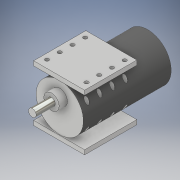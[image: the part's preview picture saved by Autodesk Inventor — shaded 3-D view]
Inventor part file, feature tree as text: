
AUTODESK INVENTOR PART (.ipt)
format: ipt  version: 2019 (Build 230136000, 136)  size: 185,856 bytes
history: native  units: in
note: dims shown in document units (in); Inventor stores cm internally (conversion verified against a paired STEP export)
features: sketch x5, extrude x4, plane x1, hole x1, pattern_linear x1, mirror x1
ambient origin geometry x8: Origin, YZ Plane, XZ Plane, XY Plane, X Axis, Y Axis, Z Axis, Center Point
bodies: Solid1 (feature_tree)
feature tree (13):
  extrude  "Extrusion1"  Depth=2.7165in TaperAngle=0.0deg
  extrude  "Extrusion2"  Depth=0.685in
  extrude  "Extrusion3"  Depth=0.2559in TaperAngle=0.0deg
  plane  "Work Plane1"
  extrude  "Extrusion4"  Depth=0.5906in TaperAngle=0.0deg
  hole  "Hole1"  [1 undecoded]
  pattern_linear  "Rectangular Pattern1"  Spacing1=1.6142in  [1 undecoded]
  mirror  "Mirror1"
  sketch  "Sketch1"  dims[d0=1.4567in d1=2.7165in d2=0.0in]
  sketch  "Sketch2"  dims[d5=0.7283in d6=0.685in]
  sketch  "Sketch3"  dims[d7=0.2362in d8=0.2559in d9=0.0in]
  sketch  "Sketch4"  dims[d10=0.2362in d11=0.5906in d12=0.0in]
  sketch  "Sketch5"  dims[d13=2.7362in d14=0.7874in d15=1.6142in d16=1.5748in d17=1.6142in d18=0.1378in d19=0.0in d20=0.1772in d21=0.2362in d22=0.3937in d23=90.0deg d24=0.1772in d25=0.2362in d26=0.1181in d27=0.146in d28=0.375in d29=0.25in d30=0.5635in d31=1.0in d32=0.8108in d33=1.5748in d35=0.3937in]
note: 2 required parameter values undecoded (feature->parameter linkage not recoverable at this tier; creation-order binding heuristic only, values carry confidence <= 0.55)
